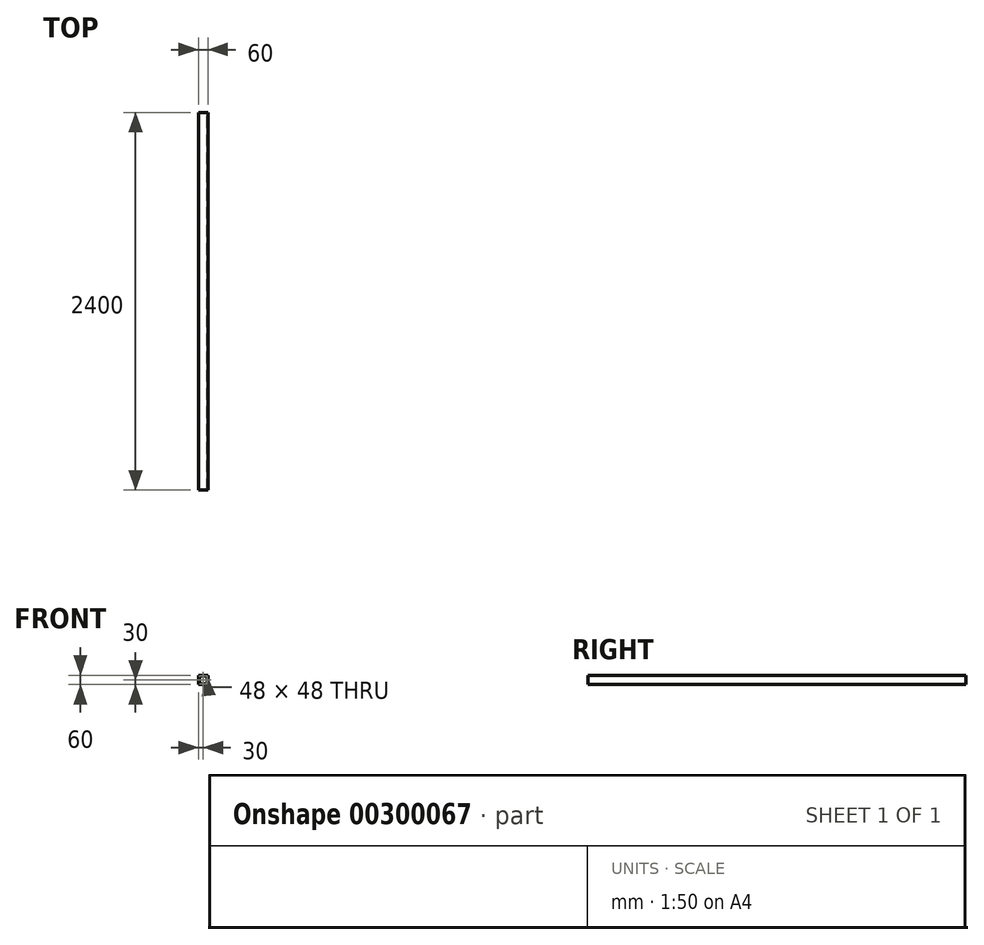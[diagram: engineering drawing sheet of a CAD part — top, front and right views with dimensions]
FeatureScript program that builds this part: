
annotation { "Feature Type Name" : "Feature", "Feature Type Description" : "" }
export const myFeature = defineFeature(function(context is Context, id is Id, definition is map)
    precondition{}
    {
        {
            var Q0;
            Q0=qCreatedBy(makeId("Front.planeOp"),FACE);
            var sketch = newSketch(context, id + "F0", { "sketchPlane" : qUnion([Q0])});
            skLineSegment(sketch, "E0.bottom", {"start": v(-30, -30) * mm, "end": v(30, -30) * mm});
            skLineSegment(sketch, "E0.top", {"start": v(-30, 30) * mm, "end": v(30, 30) * mm});
            skLineSegment(sketch, "E0.left", {"start": v(-30, -30) * mm, "end": v(-30, 30) * mm});
            skLineSegment(sketch, "E0.right", {"start": v(30, -30) * mm, "end": v(30, 30) * mm});
            skPoint(sketch, "E0.middle", {"position": v(0, 0) * mm});
            skLineSegment(sketch, "E1.bottom", {"start": v(-24, -24) * mm, "end": v(24, -24) * mm});
            skLineSegment(sketch, "E1.top", {"start": v(-24, 24) * mm, "end": v(24, 24) * mm});
            skLineSegment(sketch, "E1.left", {"start": v(-24, -24) * mm, "end": v(-24, 24) * mm});
            skLineSegment(sketch, "E1.right", {"start": v(24, -24) * mm, "end": v(24, 24) * mm});
            skSolve(sketch);
        }
        {
            var Q0;
            Q0 = qSketchRegion(id + "F0", true);
            extrude(context, id + "F1", {"entities" : qUnion([Q0]), "depth" : 2400 * mm});
        }
    });
